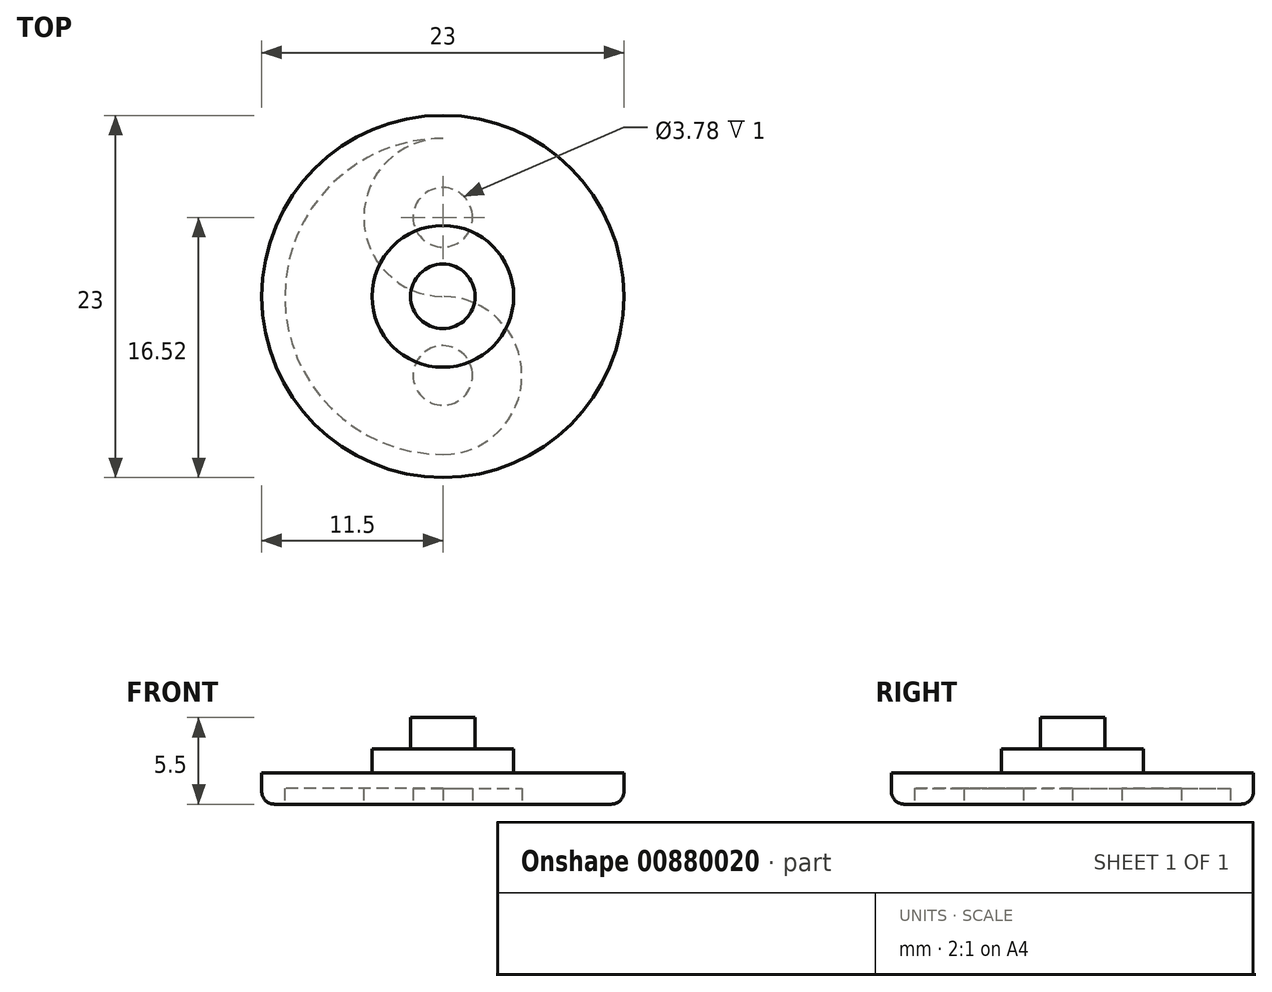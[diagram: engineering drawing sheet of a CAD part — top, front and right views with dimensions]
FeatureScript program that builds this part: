
annotation { "Feature Type Name" : "Feature", "Feature Type Description" : "" }
export const myFeature = defineFeature(function(context is Context, id is Id, definition is map)
    precondition{}
    {
        {
            var Q0;
            Q0=qCreatedBy(makeId("Top.planeOp"),FACE);
            var sketch = newSketch(context, id + "F0", { "sketchPlane" : qUnion([Q0])});
            skCircle(sketch, "E0", {"center": v(0, 0) * mm, "radius": 11.5 * mm});
            skSolve(sketch);
        }
        {
            var Q0;
            Q0=makeQuery(id+"F0.imprint","IMPRINT",FACE,{"disambiguationData":[TD([[makeQuery(id+"F0.imprint","IMPRINT",EDGE,{"derivedFrom":sQuery(id+"F0.wireOp",EDGE,"E0")}),1.0]])]});
            extrude(context, id + "F1", {"entities" : qUnion([Q0]), "depth" : 2 * mm, "offsetDistance" : 25 * mm});
        }
        {
            var Q0;
            Q0=makeQuery(id+"F1.opExtrude","CAP_FACE",FACE,{"disambiguationData":[OSD([sQuery(id+"F0.wireOp",EDGE,"E0")])],"isStart":false});
            var sketch = newSketch(context, id + "F2", { "sketchPlane" : qUnion([Q0])});
            skCircle(sketch, "E1", {"center": v(0, 0) * mm, "radius": 4.5 * mm});
            skSolve(sketch);
        }
        {
            var Q0;
            Q0=makeQuery(id+"F2.imprint","IMPRINT",FACE,{"disambiguationData":[TD([[makeQuery(id+"F2.imprint","IMPRINT",EDGE,{"derivedFrom":sQuery(id+"F2.wireOp",EDGE,"E1")}),1.0]])]});
            extrude(context, id + "F3", {"entities" : qUnion([Q0]), "operationType" : NewBodyOperationType.ADD, "depth" : 1.5 * mm, "offsetDistance" : 25 * mm});
        }
        {
            var Q0;
            Q0=makeQuery(id+"F3.opExtrude","CAP_FACE",FACE,{"disambiguationData":[OSD([sQuery(id+"F2.wireOp",EDGE,"E1")])],"isStart":false});
            var sketch = newSketch(context, id + "F4", { "sketchPlane" : qUnion([Q0])});
            skCircle(sketch, "E2", {"center": v(0, 0) * mm, "radius": 2.05 * mm});
            skSolve(sketch);
        }
        {
            var Q0;
            Q0=makeQuery(id+"F4.imprint","IMPRINT",FACE,{"disambiguationData":[TD([[makeQuery(id+"F4.imprint","IMPRINT",EDGE,{"derivedFrom":sQuery(id+"F4.wireOp",EDGE,"E2")}),1.0]])]});
            extrude(context, id + "F5", {"entities" : qUnion([Q0]), "operationType" : NewBodyOperationType.ADD, "depth" : 2 * mm, "offsetDistance" : 25 * mm});
        }
        {
            var Q0;
            Q0=makeQuery(id+"F1.opExtrude","CAP_FACE",FACE,{"disambiguationData":[OSD([sQuery(id+"F0.wireOp",EDGE,"E0")])],"isStart":true});
            var sketch = newSketch(context, id + "F6", { "sketchPlane" : qUnion([Q0])});
            skArc(sketch, "E3", {"start": v(0, 0) * mm, "mid": v(5.02, 5.02) * mm, "end": v(0, 10.04) * mm});
            skArc(sketch, "E4", {"start": v(0, 0) * mm, "mid": v(-5.02, -5.02) * mm, "end": v(0, -10.04) * mm});
            skCircle(sketch, "E5", {"center": v(0, 5.02) * mm, "radius": 1.89 * mm});
            skCircle(sketch, "E6", {"center": v(0, -5.02) * mm, "radius": 1.89 * mm});
            skArc(sketch, "E7", {"start": v(0, 10.04) * mm, "mid": v(-10.04, 0) * mm, "end": v(0, -10.04) * mm});
            skArc(sketch, "E8", {"start": v(0, -10.04) * mm, "mid": v(10.04, 0) * mm, "end": v(0, 10.04) * mm, "construction": true});
            skSolve(sketch);
        }
        {
            var Q0;
            Q0=qSketchRegion(id+"F6",true);
            extrude(context, id + "F7", {"entities" : qUnion([Q0]), "operationType" : NewBodyOperationType.REMOVE, "depth" : -1 * mm, "offsetDistance" : 25 * mm});
        }
        {
            var Q0;
            Q0=makeQuery(id+"F1.opExtrude","CAP_EDGE",EDGE,{"disambiguationData":[OSD([sQuery(id+"F0.wireOp",EDGE,"E0")])],"isStart":true});
            fillet(context, id + "F8", {"entities" : qUnion([Q0]), "radius" : .8 * mm, "tangentPropagation" : true, "allowEdgeOverflow" : false});
        }
    });
